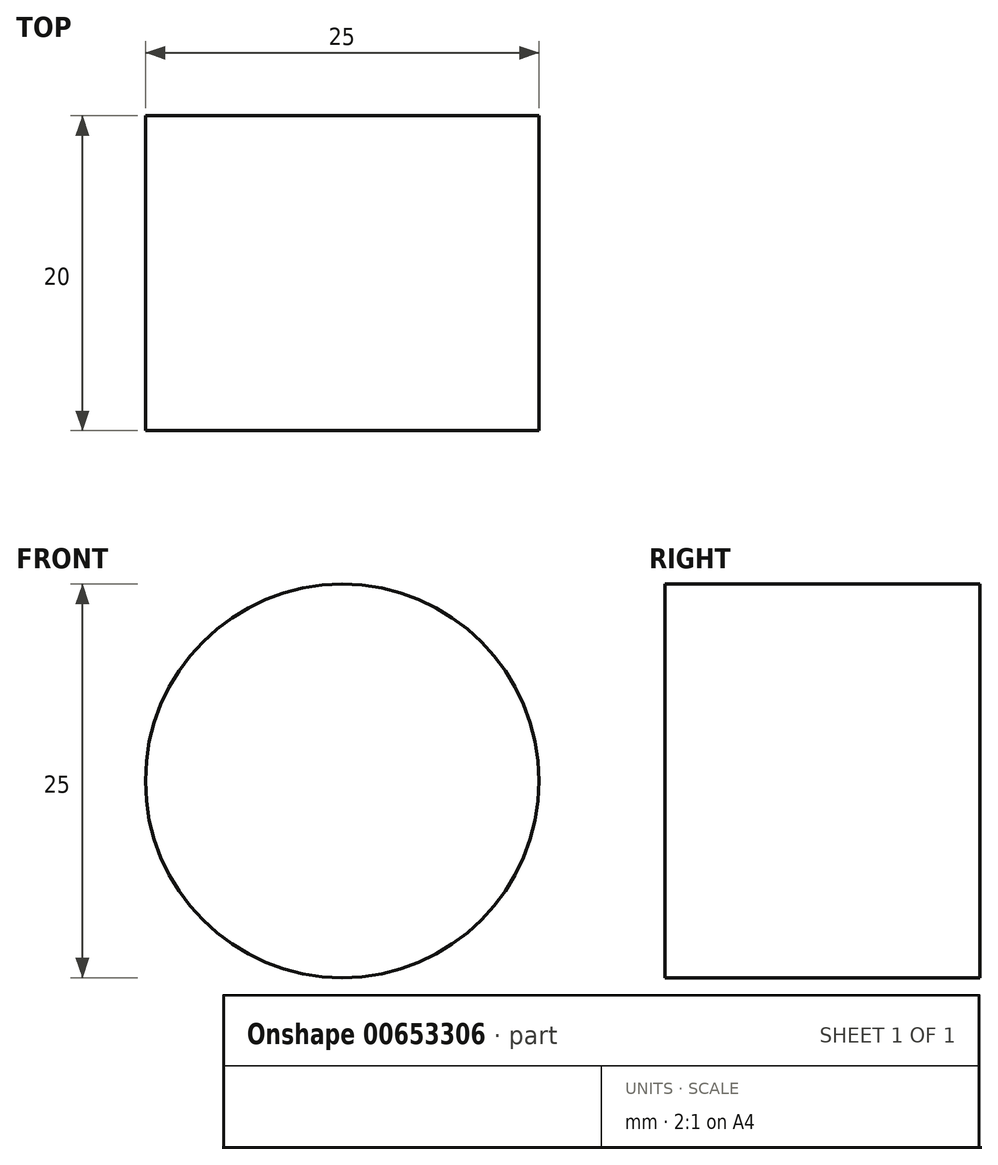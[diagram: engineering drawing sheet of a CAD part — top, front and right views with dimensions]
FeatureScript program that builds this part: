
annotation { "Feature Type Name" : "Feature", "Feature Type Description" : "" }
export const myFeature = defineFeature(function(context is Context, id is Id, definition is map)
    precondition{}
    {
        {
            var Q0;
            Q0=qCreatedBy(makeId("Front.planeOp"),FACE);
            var sketch = newSketch(context, id + "F0", { "sketchPlane" : qUnion([Q0])});
            skCircle(sketch, "E0", {"center": v(0, 0) * mm, "radius": 12.5 * mm});
            skCircle(sketch, "E1.cCircle", {"center": v(0, 0) * mm, "radius": 12.5 * mm, "construction": true});
            skLineSegment(sketch, "E1.0", {"start": v(11.89, -3.86) * mm, "end": v(0, -12.5) * mm, "construction": true});
            skLineSegment(sketch, "E1.1", {"start": v(0, -12.5) * mm, "end": v(-11.89, -3.86) * mm, "construction": true});
            skLineSegment(sketch, "E1.2", {"start": v(-11.89, -3.86) * mm, "end": v(-7.35, 10.11) * mm, "construction": true});
            skLineSegment(sketch, "E1.3", {"start": v(-7.35, 10.11) * mm, "end": v(7.35, 10.11) * mm, "construction": true});
            skLineSegment(sketch, "E1.4", {"start": v(7.35, 10.11) * mm, "end": v(11.89, -3.86) * mm, "construction": true});
            skLineSegment(sketch, "E2", {"start": v(0, 0) * mm, "end": v(0, -12.5) * mm});
            skSolve(sketch);
        }
        {
            var Q0;
            Q0=makeQuery(id+"F0.imprint","IMPRINT",FACE,{"disambiguationData":[TD([[makeQuery(id+"F0.imprint","IMPRINT",EDGE,{"derivedFrom":sQuery(id+"F0.wireOp",EDGE,"E0")}),1.0]])]});
            extrude(context, id + "F1", {"entities" : qUnion([Q0]), "depth" : 20 * mm, "offsetDistance" : 25 * mm});
        }
    });
